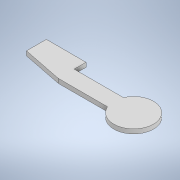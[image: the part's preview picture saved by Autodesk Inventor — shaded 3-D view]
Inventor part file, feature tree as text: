
AUTODESK INVENTOR PART (.ipt)
format: ipt  version: 2022 (Build 260153000, 153)  size: 135,680 bytes
history: native  units: mm
features: extrude x4, sketch x3, other x1, projected_geometry x1
ambient origin geometry x8: Origin, YZ Plane, XZ Plane, XY Plane, X Axis, Y Axis, Z Axis, Center Point
bodies: Body1 (feature_tree)
feature tree (9):
  other  "Sólido1"
  sketch  "Boceto1"  dims[d0=100.0mm d1=20.0mm]
  extrude  "Extrusión1"  Depth=20.0mm
  extrude  "Extrusión2"  Depth=5.5mm TaperAngle=0.0deg
  extrude  "Extrusión8"  Depth=50.0mm
  extrude  "Extrusión9"  Depth=5.5mm TaperAngle=0.0deg
  sketch  "Boceto5"  dims[d2=30.0mm d3=5.5mm d4=0.0mm]
  sketch  "Boceto6"  dims[d5=5.5mm d6=0.0mm d27=50.0mm d28=5.5mm d29=0.0mm d33=50.0mm d34=50.0mm d35=5.5mm d36=0.0mm d31=0.5mm d32=0.872665mm]
  projected_geometry  "Contorno proyectado1"
